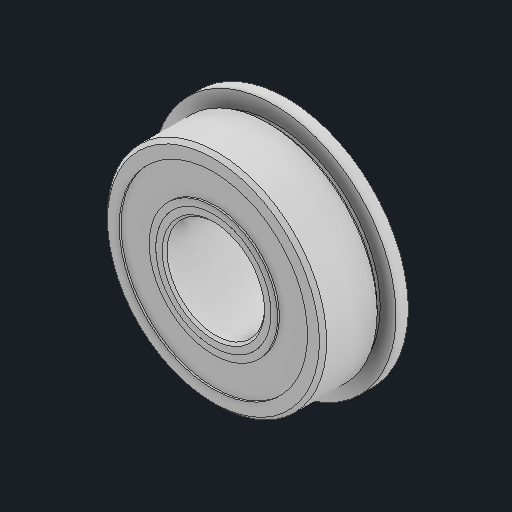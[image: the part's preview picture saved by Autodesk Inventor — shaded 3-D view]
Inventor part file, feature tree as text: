
AUTODESK INVENTOR PART (.ipt)
format: ipt  version: 2024 (Build 280153000, 153)  size: 652,800 bytes
history: native  units: in
note: dims shown in document units (in); Inventor stores cm internally (conversion verified against a paired STEP export)
features: other x14, revolve x3
ambient origin geometry x8: Origin, YZ Plane, XZ Plane, XY Plane, X Axis, Y Axis, Z Axis, Center Point
bodies: Solid1 (feature_tree), Solid2 (feature_tree), Solid3 (feature_tree), Solid4 (feature_tree), Solid5 (feature_tree), Solid6 (feature_tree), Solid7 (feature_tree), Solid8 (feature_tree), Solid9 (feature_tree), Solid10 (feature_tree), Solid11 (feature_tree), Solid12 (feature_tree), Solid13 (feature_tree), Solid14 (feature_tree), Solid15 (feature_tree), Solid16 (feature_tree), Solid17 (feature_tree)
feature tree (17):
  revolve  "Revolve2"  [1 undecoded]
  revolve  "Revolve4"  [1 undecoded]
  other  "Cut-Revolve1"
  revolve  "Revolve6[1]"  [1 undecoded]
  other  "CirPattern1[1]"
  other  "CirPattern1[2]"
  other  "CirPattern1[3]"
  other  "CirPattern1[4]"
  other  "CirPattern1[5]"
  other  "CirPattern1[6]"
  other  "CirPattern1[7]"
  other  "CirPattern1[8]"
  other  "CirPattern1[9]"
  other  "CirPattern1[10]"
  other  "CirPattern1[11]"
  other  "Cut-Extrude1"
  other  "Cut-Extrude2"
note: 3 required parameter values undecoded (feature->parameter linkage not recoverable at this tier; creation-order binding heuristic only, values carry confidence <= 0.55)
